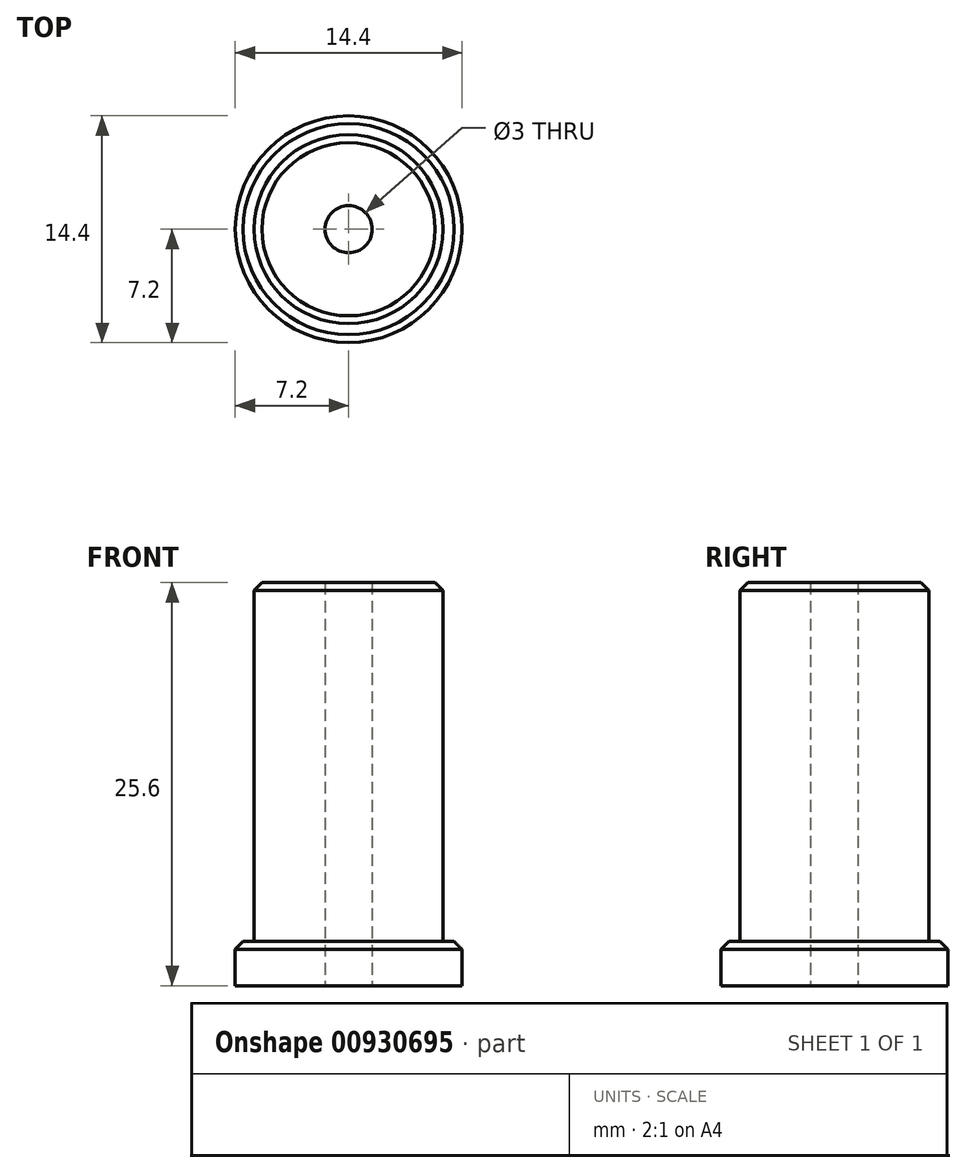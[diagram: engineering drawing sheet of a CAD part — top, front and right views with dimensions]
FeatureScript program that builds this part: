
annotation { "Feature Type Name" : "Feature", "Feature Type Description" : "" }
export const myFeature = defineFeature(function(context is Context, id is Id, definition is map)
    precondition{}
    {
        {
            var Q0;
            Q0=qCreatedBy(makeId("Front.planeOp"),FACE);
            var sketch = newSketch(context, id + "F0", { "sketchPlane" : qUnion([Q0])});
            skLineSegment(sketch, "E0", {"start": v(0, 0) * mm, "end": v(0, 25) * mm, "construction": true});
            skLineSegment(sketch, "E1", {"start": v(7.2, 0) * mm, "end": v(7.2, 2.8) * mm});
            skLineSegment(sketch, "E2", {"start": v(7.2, 2.8) * mm, "end": v(6, 2.8) * mm});
            skLineSegment(sketch, "E3", {"start": v(6, 2.8) * mm, "end": v(6, 25.6) * mm});
            skLineSegment(sketch, "E4", {"start": v(6, 25.6) * mm, "end": v(1.5, 25.6) * mm});
            skLineSegment(sketch, "E5", {"start": v(1.5, 25.6) * mm, "end": v(1.5, 0) * mm});
            skLineSegment(sketch, "E6", {"start": v(1.5, 0) * mm, "end": v(7.2, 0) * mm});
            skSolve(sketch);
        }
        {
            var Q0;
            Q0=qSketchRegion(id+"F0",true);
            var Q1;
            Q1=sQuery(id+"F0.wireOp",EDGE,"E0");
            revolve(context, id + "F1", {"entities" : qUnion([Q0]), "axis" : qUnion([Q1]), "revolveType" : RevolveType.FULL});
        }
        {
            var Q0;
            Q0=makeQuery(id+"F1.opRevolve","SWEPT_EDGE",EDGE,{"disambiguationData":[OSD([sQuery(id+"F0.wireOp",EDGE,"E1"),sQuery(id+"F0.wireOp",EDGE,"E2")])]});
            var Q1;
            Q1=makeQuery(id+"F1.opRevolve","SWEPT_EDGE",EDGE,{"disambiguationData":[OSD([sQuery(id+"F0.wireOp",EDGE,"E3"),sQuery(id+"F0.wireOp",EDGE,"E4")])]});
            chamfer(context, id + "F2", {"entities" : qUnion([Q0, Q1]), "width" : 0.5 * mm, "tangentPropagation" : true});
        }
    });
